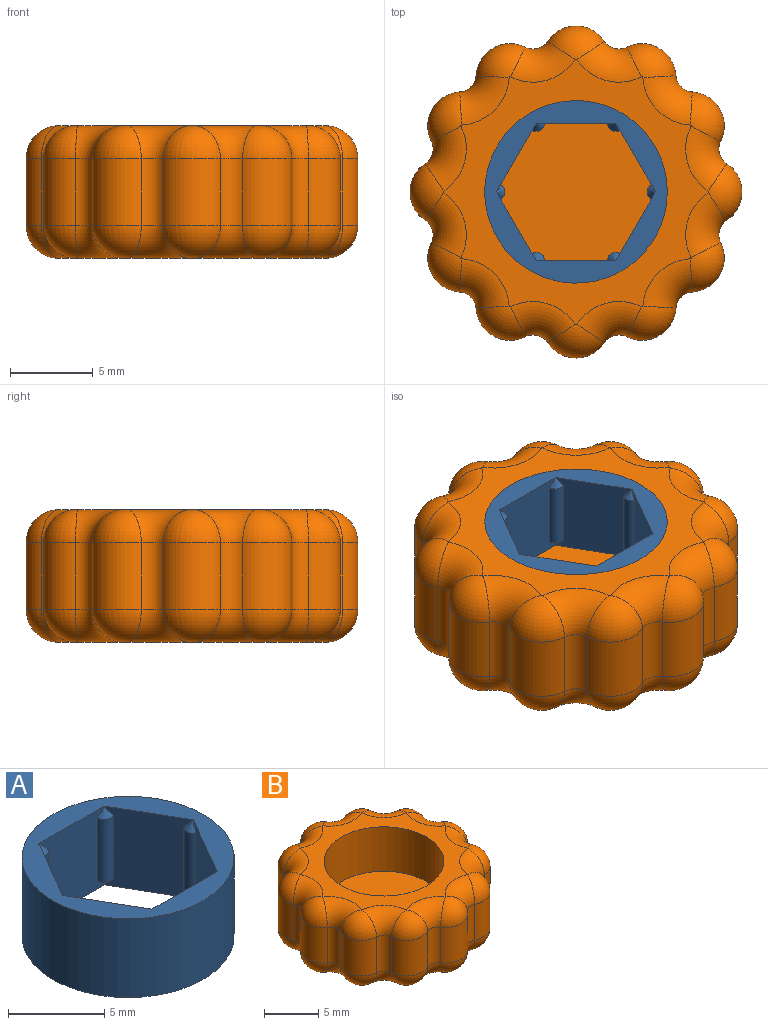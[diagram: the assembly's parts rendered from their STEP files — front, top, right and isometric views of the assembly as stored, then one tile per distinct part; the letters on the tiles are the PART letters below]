
ASSEMBLY  parts=2 mates=1
PART A: 27 faces, bbox 11x11x5 mm
  f0: plane 5x4.15mm, normal (0.87,-0.5,0), area 19.5mm2, adj f7,f8,f21,f22,f23,f24,f25,f26
  f1: plane 5x4.79mm, normal (0,-1,0), area 19.5mm2, adj f7,f8,f9,f10,f11,f21,f22,f23
  f2: plane 5x4.15mm, normal (-0.87,-0.5,0), area 19.5mm2, adj f7,f8,f9,f10,f11,f15,f16,f17
  f3: plane 5x4.15mm, normal (-0.87,0.5,0), area 19.5mm2, adj f7,f8,f12,f13,f14,f15,f16,f17
  f4: plane 5x4.79mm, normal (0,1,0), area 19.5mm2, adj f7,f8,f12,f13,f14,f18,f19,f20
  f5: plane 5x4.15mm, normal (0.87,0.5,0), area 19.5mm2, adj f7,f8,f18,f19,f20,f24,f25,f26
  f6: cylinder r=5.5mm len=11mm, axis (0,0,-1), area 172.8mm2, adj f7,f8
  f7: plane 11x11mm, normal (0,0,1), area 35.4mm2, adj f0,f1,f2,f3,f4,f5,f6
  f8: plane 11x11mm, normal (0,0,-1), area 35.4mm2, adj f0,f1,f2,f3,f4,f5,f6
  f9: cylinder r=0.5mm len=4mm, axis (0,0,-1), area 4.2mm2, adj f1,f2,f10,f11
  f10: cone r=0.5mm half-angle=45deg, axis (0,0,-1), area 0.4mm2, adj f1,f2,f9
  f11: cone r=0.5mm half-angle=45deg, axis (0,0,1), area 0.4mm2, adj f1,f2,f9
  f12: cylinder r=0.5mm len=4mm, axis (0,0,-1), area 4.2mm2, adj f3,f4,f13,f14
  f13: cone r=0.5mm half-angle=45deg, axis (0,0,-1), area 0.4mm2, adj f3,f4,f12
  f14: cone r=0.5mm half-angle=45deg, axis (0,0,1), area 0.4mm2, adj f3,f4,f12
  f15: cylinder r=0.5mm len=4mm, axis (0,0,-1), area 4.2mm2, adj f2,f3,f16,f17
  f16: cone r=0.5mm half-angle=45deg, axis (0,0,-1), area 0.4mm2, adj f2,f3,f15
  f17: cone r=0.5mm half-angle=45deg, axis (0,0,1), area 0.4mm2, adj f2,f3,f15
  f18: cylinder r=0.5mm len=4mm, axis (0,0,-1), area 4.2mm2, adj f4,f5,f19,f20
  f19: cone r=0.5mm half-angle=45deg, axis (0,0,-1), area 0.4mm2, adj f4,f5,f18
  f20: cone r=0.5mm half-angle=45deg, axis (0,0,1), area 0.4mm2, adj f4,f5,f18
  f21: cylinder r=0.5mm len=4mm, axis (0,0,-1), area 4.2mm2, adj f0,f1,f22,f23
  f22: cone r=0.5mm half-angle=45deg, axis (0,0,-1), area 0.4mm2, adj f0,f1,f21
  f23: cone r=0.5mm half-angle=45deg, axis (0,0,1), area 0.4mm2, adj f0,f1,f21
  f24: cylinder r=0.5mm len=4mm, axis (0,0,-1), area 4.2mm2, adj f0,f5,f25,f26
  f25: cone r=0.5mm half-angle=45deg, axis (0,0,-1), area 0.4mm2, adj f0,f5,f24
  f26: cone r=0.5mm half-angle=45deg, axis (0,0,1), area 0.4mm2, adj f0,f5,f24
PART B: 76 faces, bbox 20x20x8 mm
  f0: plane 16x16mm, normal (0,0,1), area 71mm2, adj f26,f52,f53,f54,f55,f56,f57,f58
  f1: plane 16x16mm, normal (0,0,-1), area 166mm2, adj f28,f29,f30,f31,f32,f33,f34,f35
  f2: cylinder r=2.06mm len=4mm, axis (0,0,1), area 16.2mm2, adj f3,f6,f44,f55
  f3: cylinder r=1.05mm len=4mm, axis (0,0,1), area 6.1mm2, adj f2,f4,f42,f53
  f4: cylinder r=2.06mm len=4mm, axis (0,0,1), area 16.2mm2, adj f3,f25,f40,f52
  f5: cylinder r=2.06mm len=4mm, axis (0,0,1), area 16.2mm2, adj f6,f8,f48,f59
  f6: cylinder r=1.05mm len=4mm, axis (0,0,1), area 6.1mm2, adj f2,f5,f46,f57
  f7: cylinder r=2.06mm len=4mm, axis (0,0,1), area 16.2mm2, adj f8,f10,f51,f63
  f8: cylinder r=1.05mm len=4mm, axis (0,0,1), area 6.1mm2, adj f5,f7,f50,f61
  f9: cylinder r=2.06mm len=4mm, axis (0,0,1), area 16.2mm2, adj f10,f12,f47,f67
  f10: cylinder r=1.05mm len=4mm, axis (0,0,1), area 6.1mm2, adj f7,f9,f49,f65
  f11: cylinder r=2.06mm len=4mm, axis (0,0,1), area 16.2mm2, adj f12,f14,f43,f71
  f12: cylinder r=1.05mm len=4mm, axis (0,0,1), area 6.1mm2, adj f9,f11,f45,f69
  f13: cylinder r=2.06mm len=4mm, axis (0,0,1), area 16.2mm2, adj f14,f16,f39,f75
  f14: cylinder r=1.05mm len=4mm, axis (0,0,1), area 6.1mm2, adj f11,f13,f41,f73
  f15: cylinder r=2.06mm len=4mm, axis (0,0,1), area 16.2mm2, adj f16,f18,f35,f72
  f16: cylinder r=1.05mm len=4mm, axis (0,0,1), area 6.1mm2, adj f13,f15,f37,f74
  f17: cylinder r=2.06mm len=4mm, axis (0,0,1), area 16.2mm2, adj f18,f20,f31,f68
  f18: cylinder r=1.05mm len=4mm, axis (0,0,1), area 6.1mm2, adj f15,f17,f33,f70
  f19: cylinder r=2.06mm len=4mm, axis (0,0,1), area 16.2mm2, adj f20,f22,f28,f64
  f20: cylinder r=1.05mm len=4mm, axis (0,0,1), area 6.1mm2, adj f17,f19,f29,f66
  f21: cylinder r=2.06mm len=4mm, axis (0,0,1), area 16.2mm2, adj f22,f24,f32,f60
  f22: cylinder r=1.05mm len=4mm, axis (0,0,1), area 6.1mm2, adj f19,f21,f30,f62
  f23: cylinder r=2.06mm len=4mm, axis (0,0,1), area 16.2mm2, adj f24,f25,f36,f56
  f24: cylinder r=1.05mm len=4mm, axis (0,0,1), area 6.1mm2, adj f21,f23,f34,f58
  f25: cylinder r=1.05mm len=4mm, axis (0,0,1), area 6.1mm2, adj f4,f23,f38,f54
  f26: cylinder r=5.5mm len=11mm, axis (0,0,1), area 172.8mm2, adj f0,f27
  f27: plane 11x11mm, normal (0,0,1), area 95mm2, adj f26
  f28: torus R=0.06mm, axis (0,0,1), area 8.2mm2, adj f1,f19,f29,f30
  f29: torus R=3.05mm, axis (0,0,1), area 8.1mm2, adj f1,f20,f28,f31
  f30: torus R=3.05mm, axis (0,0,1), area 8.1mm2, adj f1,f22,f28,f32
  f31: torus R=0.06mm, axis (0,0,1), area 8.2mm2, adj f1,f17,f29,f33
  f32: torus R=0.06mm, axis (0,0,1), area 8.2mm2, adj f1,f21,f30,f34
  f33: torus R=3.05mm, axis (0,0,1), area 8.1mm2, adj f1,f18,f31,f35
  f34: torus R=3.05mm, axis (0,0,1), area 8.1mm2, adj f1,f24,f32,f36
  f35: torus R=0.06mm, axis (0,0,1), area 8.2mm2, adj f1,f15,f33,f37
  f36: torus R=0.06mm, axis (0,0,1), area 8.2mm2, adj f1,f23,f34,f38
  f37: torus R=3.05mm, axis (0,0,1), area 8.1mm2, adj f1,f16,f35,f39
  f38: torus R=3.05mm, axis (0,0,1), area 8.1mm2, adj f1,f25,f36,f40
  f39: torus R=0.06mm, axis (0,0,1), area 8.2mm2, adj f1,f13,f37,f41
  f40: torus R=0.06mm, axis (0,0,1), area 8.2mm2, adj f1,f4,f38,f42
  f41: torus R=3.05mm, axis (0,0,1), area 8.1mm2, adj f1,f14,f39,f43
  f42: torus R=3.05mm, axis (0,0,1), area 8.1mm2, adj f1,f3,f40,f44
  f43: torus R=0.06mm, axis (0,0,1), area 8.2mm2, adj f1,f11,f41,f45
  f44: torus R=0.06mm, axis (0,0,1), area 8.2mm2, adj f1,f2,f42,f46
  f45: torus R=3.05mm, axis (0,0,1), area 8.1mm2, adj f1,f12,f43,f47
  f46: torus R=3.05mm, axis (0,0,1), area 8.1mm2, adj f1,f6,f44,f48
  f47: torus R=0.06mm, axis (0,0,1), area 8.2mm2, adj f1,f9,f45,f49
  f48: torus R=0.06mm, axis (0,0,1), area 8.2mm2, adj f1,f5,f46,f50
  f49: torus R=3.05mm, axis (0,0,1), area 8.1mm2, adj f1,f10,f47,f51
  f50: torus R=3.05mm, axis (0,0,1), area 8.1mm2, adj f1,f8,f48,f51
  f51: torus R=0.06mm, axis (0,0,1), area 8.2mm2, adj f1,f7,f49,f50
  f52: torus R=0.06mm, axis (0,0,1), area 8.2mm2, adj f0,f4,f53,f54
  f53: torus R=3.05mm, axis (0,0,1), area 8.1mm2, adj f0,f3,f52,f55
  f54: torus R=3.05mm, axis (0,0,1), area 8.1mm2, adj f0,f25,f52,f56
  f55: torus R=0.06mm, axis (0,0,1), area 8.2mm2, adj f0,f2,f53,f57
  f56: torus R=0.06mm, axis (0,0,1), area 8.2mm2, adj f0,f23,f54,f58
  f57: torus R=3.05mm, axis (0,0,1), area 8.1mm2, adj f0,f6,f55,f59
  f58: torus R=3.05mm, axis (0,0,1), area 8.1mm2, adj f0,f24,f56,f60
  f59: torus R=0.06mm, axis (0,0,1), area 8.2mm2, adj f0,f5,f57,f61
  f60: torus R=0.06mm, axis (0,0,1), area 8.2mm2, adj f0,f21,f58,f62
  f61: torus R=3.05mm, axis (0,0,1), area 8.1mm2, adj f0,f8,f59,f63
  f62: torus R=3.05mm, axis (0,0,1), area 8.1mm2, adj f0,f22,f60,f64
  f63: torus R=0.06mm, axis (0,0,1), area 8.2mm2, adj f0,f7,f61,f65
  f64: torus R=0.06mm, axis (0,0,1), area 8.2mm2, adj f0,f19,f62,f66
  f65: torus R=3.05mm, axis (0,0,1), area 8.1mm2, adj f0,f10,f63,f67
  f66: torus R=3.05mm, axis (0,0,1), area 8.1mm2, adj f0,f20,f64,f68
  f67: torus R=0.06mm, axis (0,0,1), area 8.2mm2, adj f0,f9,f65,f69
  f68: torus R=0.06mm, axis (0,0,1), area 8.2mm2, adj f0,f17,f66,f70
  f69: torus R=3.05mm, axis (0,0,1), area 8.1mm2, adj f0,f12,f67,f71
  f70: torus R=3.05mm, axis (0,0,1), area 8.1mm2, adj f0,f18,f68,f72
  f71: torus R=0.06mm, axis (0,0,1), area 8.2mm2, adj f0,f11,f69,f73
  f72: torus R=0.06mm, axis (0,0,1), area 8.2mm2, adj f0,f15,f70,f74
  f73: torus R=3.05mm, axis (0,0,1), area 8.1mm2, adj f0,f14,f71,f75
  f74: torus R=3.05mm, axis (0,0,1), area 8.1mm2, adj f0,f16,f72,f75
  f75: torus R=0.06mm, axis (0,0,1), area 8.2mm2, adj f0,f13,f73,f74
PLACE A t=(7.72,-10.47,7.93)mm
PLACE B t=(7.72,-10.47,4.93)mm
MATE fastened B.f26 <-> A.f6  axis (0,0,1) through (7.72,-10.47,7.93)mm
